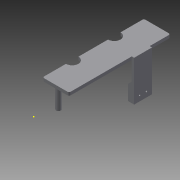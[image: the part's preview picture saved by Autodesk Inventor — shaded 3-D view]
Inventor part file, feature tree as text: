
AUTODESK INVENTOR PART (.ipt)
format: ipt  version: 2015 SP2 (Build 190223200, 223)  size: 193,024 bytes
history: native  units: in
note: dims shown in document units (in); Inventor stores cm internally (conversion verified against a paired STEP export)
features: sketch x19, extrude x9, fillet x1, hole x1
ambient origin geometry x8: Origin, YZ Plane, XZ Plane, XY Plane, X Axis, Y Axis, Z Axis, Center Point
bodies: Body1 (feature_tree)
feature tree (30):
  extrude  "Extrusion4"  Depth=0.6693in
  fillet  "Fillet1"  Radius=0.0787in
  sketch  "Sketch14"  dims[d44=0.0394in d46=0.5315in]
  extrude  "Extrusion8"  Depth=0.0394in
  extrude  "Extrusion9"  Depth=0.1969in TaperAngle=0.0deg
  sketch  "Sketch17"  dims[d52=0.1181in d53=0.5906in d54=0.0in]
  sketch  "Sketch19"  dims[d55=0.1575in d56=0.1575in]
  sketch  "Sketch25"  dims[d57=0.4563in d93=0.0591in d94=0.0in]
  extrude  "Extrusion16"  Depth=0.4698in
  extrude  "Extrusion17"  Depth=0.5906in TaperAngle=0.0deg
  hole  "Hole4"  [1 undecoded]
  sketch  "Sketch30"  dims[d115=0.0394in d116=0.0in]
  sketch  "Sketch31"  dims[d117=0.0394in d118=0.0in]
  sketch  "Sketch35"  dims[d119=0.0197in d120=0.0in]
  sketch  "Sketch36"
  sketch  "Sketch37"
  extrude  "Extrusion21"  Depth=0.0591in TaperAngle=0.0deg
  sketch  "Sketch38"
  sketch  "Sketch39"
  extrude  "Extrusion22"  Depth=0.0394in
  extrude  "Extrusion23"  Depth=0.0787in
  extrude  "Extrusion24"  Depth=0.4527in TaperAngle=0.0deg
  sketch  "Sketch41"
  sketch  "Sketch7"  dims[d16=2.5591in d17=0.6693in d18=0.0787in d19=0.0in]
  sketch  "Sketch15"  dims[d47=0.315in d48=0.1969in d49=0.0in]
  sketch  "Sketch16"  dims[d50=0.6188in d51=0.4698in]
  sketch  "Sketch27"  dims[d95=0.9449in d96=0.0in d97=0.0394in]
  sketch  "Sketch28"  dims[d98=0.0394in d99=0.2362in d100=0.1575in d101=0.0787in d102=90.0deg d103=0.315in d104=0.8108in d111=0.4724in]
  sketch  "Sketch29"  dims[d112=45.0deg d113=0.4527in d114=0.0in]
  sketch  "Sketch40"
note: 1 required parameter value undecoded (feature->parameter linkage not recoverable at this tier; creation-order binding heuristic only, values carry confidence <= 0.55)
